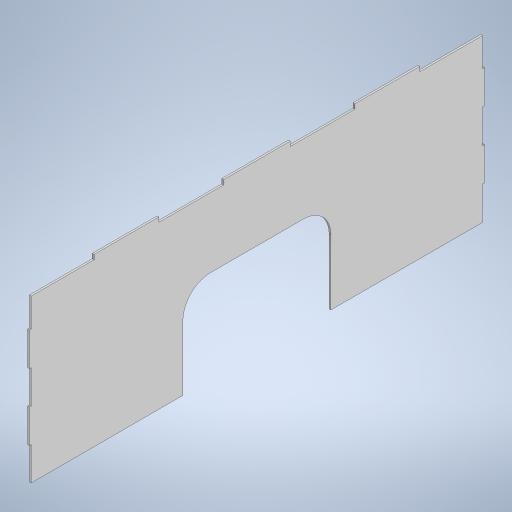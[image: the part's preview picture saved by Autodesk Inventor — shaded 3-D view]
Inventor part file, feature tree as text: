
AUTODESK INVENTOR PART (.ipt)
format: ipt  version: 2023 (Build 270158000, 158)  size: 282,624 bytes
history: native  units: mm
features: extrude x3, sketch x3
ambient origin geometry x8: Origin, YZ Plane, XZ Plane, XY Plane, X Axis, Y Axis, Z Axis, Center Point
bodies: Solid1 (feature_tree)
feature tree (6):
  extrude  "Extrusion1"  Depth=492.0mm
  extrude  "Extrusion2"  Depth=160.0mm
  extrude  "Extrusion3"  Depth=100.0mm
  sketch  "Sketch1"  dims[d0=180.0mm d1=492.0mm]
  sketch  "Sketch2"  dims[d2=100.0mm d3=160.0mm]
  sketch  "Sketch3"  dims[d4=166.0mm d5=100.0mm d6=2.0mm d7=0.0mm d8=30.0mm d9=70.0mm d10=70.0mm d11=70.0mm d12=70.0mm d13=0.0mm d14=70.0mm d15=70.0mm d16=72.0mm d17=5.0mm d18=2.0mm d19=0.0mm d20=36.0mm d21=36.0mm d22=36.0mm d23=36.0mm d24=2.0mm d25=2.0mm d26=36.0mm d27=36.0mm d28=36.0mm d29=36.0mm d30=2.0mm d31=0.0mm]
